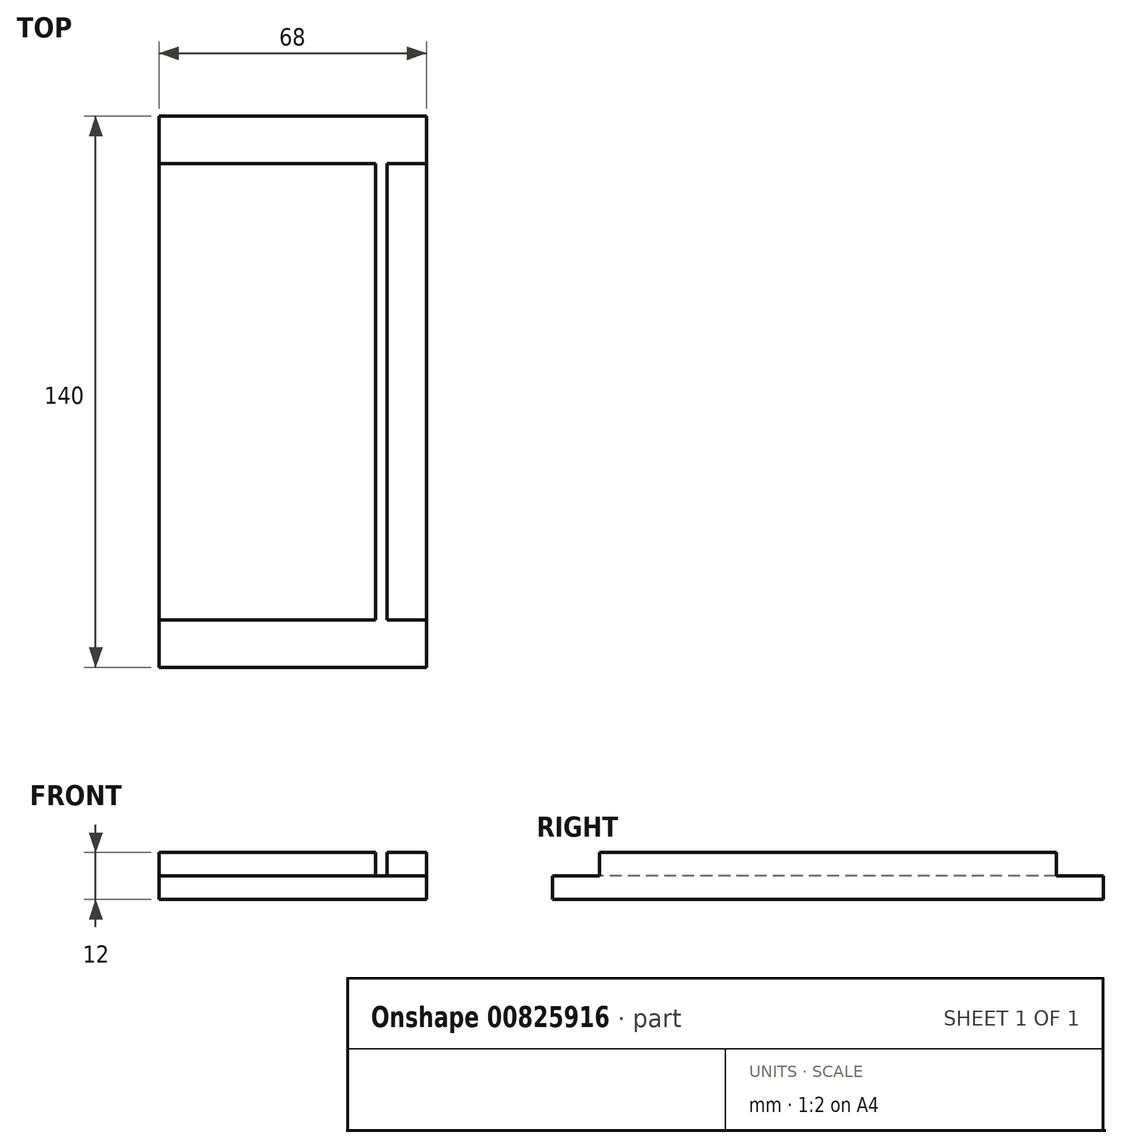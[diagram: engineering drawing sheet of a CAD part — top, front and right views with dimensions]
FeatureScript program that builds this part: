
annotation { "Feature Type Name" : "Feature", "Feature Type Description" : "" }
export const myFeature = defineFeature(function(context is Context, id is Id, definition is map)
    precondition{}
    {
        {
            var Q0;
            Q0=qCreatedBy(makeId("Front.planeOp"),FACE);
            var sketch = newSketch(context, id + "F0", { "sketchPlane" : qUnion([Q0])});
            skLineSegment(sketch, "E0.bottom", {"start": v(34, 6) * mm, "end": v(-34, 6) * mm});
            skLineSegment(sketch, "E0.top", {"start": v(34, -6) * mm, "end": v(-34, -6) * mm});
            skLineSegment(sketch, "E0.left", {"start": v(34, 6) * mm, "end": v(34, -6) * mm});
            skLineSegment(sketch, "E0.right", {"start": v(-34, 6) * mm, "end": v(-34, -6) * mm});
            skPoint(sketch, "E0.middle", {"position": v(0, 0) * mm});
            skSolve(sketch);
        }
        {
            var Q0;
            Q0=makeQuery(id+"F0.imprint","IMPRINT",FACE,{"disambiguationData":[TD([[makeQuery(id+"F0.imprint","IMPRINT",EDGE,{"derivedFrom":sQuery(id+"F0.wireOp",EDGE,"E0.bottom")}),1.0]])]});
            extrude(context, id + "F1", {"entities" : qUnion([Q0]), "depth" : 140 * mm, "offsetDistance" : 25 * mm});
        }
        {
            var Q0;
            Q0=makeQuery(id+"F1.opExtrude","CAP_FACE",FACE,{"disambiguationData":[OSD([sQuery(id+"F0.wireOp",EDGE,"E0.bottom"),sQuery(id+"F0.wireOp",EDGE,"E0.top"),sQuery(id+"F0.wireOp",EDGE,"E0.left"),sQuery(id+"F0.wireOp",EDGE,"E0.right")])],"isStart":false});
            var sketch = newSketch(context, id + "F2", { "sketchPlane" : qUnion([Q0])});
            skLineSegment(sketch, "E1", {"start": v(21, 6) * mm, "end": v(21, 0) * mm});
            skLineSegment(sketch, "E2", {"start": v(21, 0) * mm, "end": v(24, 0) * mm});
            skLineSegment(sketch, "E3", {"start": v(24, 0) * mm, "end": v(24, 6) * mm});
            skSolve(sketch);
        }
        {
            var Q0;
            {var subQ0=sQuery(id+"F2.wireOp",EDGE,"E1");Q0=makeQuery(id+"F2.imprint","IMPRINT",FACE,{"disambiguationData":[TD([[makeQuery(id+"F2.imprint","IMPRINT",EDGE,{"derivedFrom":subQ0}),1.0]])]});}
            extrude(context, id + "F3", {"entities" : qUnion([Q0]), "operationType" : NewBodyOperationType.REMOVE, "oppositeDirection" : true, "depth" : 140 * mm, "offsetDistance" : 25 * mm});
        }
        {
            var Q0;
            Q0=makeQuery(id+"F1.opExtrude","SWEPT_FACE",FACE,{"disambiguationData":[OSD([sQuery(id+"F0.wireOp",EDGE,"E0.right")])]});
            var sketch = newSketch(context, id + "F4", { "sketchPlane" : qUnion([Q0])});
            skLineSegment(sketch, "E4", {"start": v(12, 6) * mm, "end": v(12, 0) * mm});
            skLineSegment(sketch, "E5", {"start": v(12, 0) * mm, "end": v(0, 0) * mm});
            skLineSegment(sketch, "E6", {"start": v(0, 0) * mm, "end": v(0, 6) * mm});
            skLineSegment(sketch, "E7", {"start": v(0, 6) * mm, "end": v(12, 6) * mm});
            skLineSegment(sketch, "E8", {"start": v(128, 6) * mm, "end": v(128, 0) * mm});
            skLineSegment(sketch, "E9", {"start": v(128, 0) * mm, "end": v(140, 0) * mm});
            skLineSegment(sketch, "E10", {"start": v(140, 0) * mm, "end": v(140, 6) * mm});
            skLineSegment(sketch, "E11", {"start": v(140, 6) * mm, "end": v(128, 6) * mm});
            skSolve(sketch);
        }
        {
            var Q0;
            Q0=makeQuery(id+"F4.imprint","IMPRINT",FACE,{"disambiguationData":[TD([[makeQuery(id+"F4.imprint","IMPRINT",EDGE,{"derivedFrom":sQuery(id+"F4.wireOp",EDGE,"E4")}),-1.0]])]});
            var Q1;
            Q1=makeQuery(id+"F4.imprint","IMPRINT",FACE,{"disambiguationData":[TD([[makeQuery(id+"F4.imprint","IMPRINT",EDGE,{"derivedFrom":sQuery(id+"F4.wireOp",EDGE,"E8")}),1.0]])]});
            extrude(context, id + "F5", {"entities" : qUnion([Q0, Q1]), "operationType" : NewBodyOperationType.REMOVE, "oppositeDirection" : true, "depth" : 70 * mm, "offsetDistance" : 25 * mm});
        }
    });
